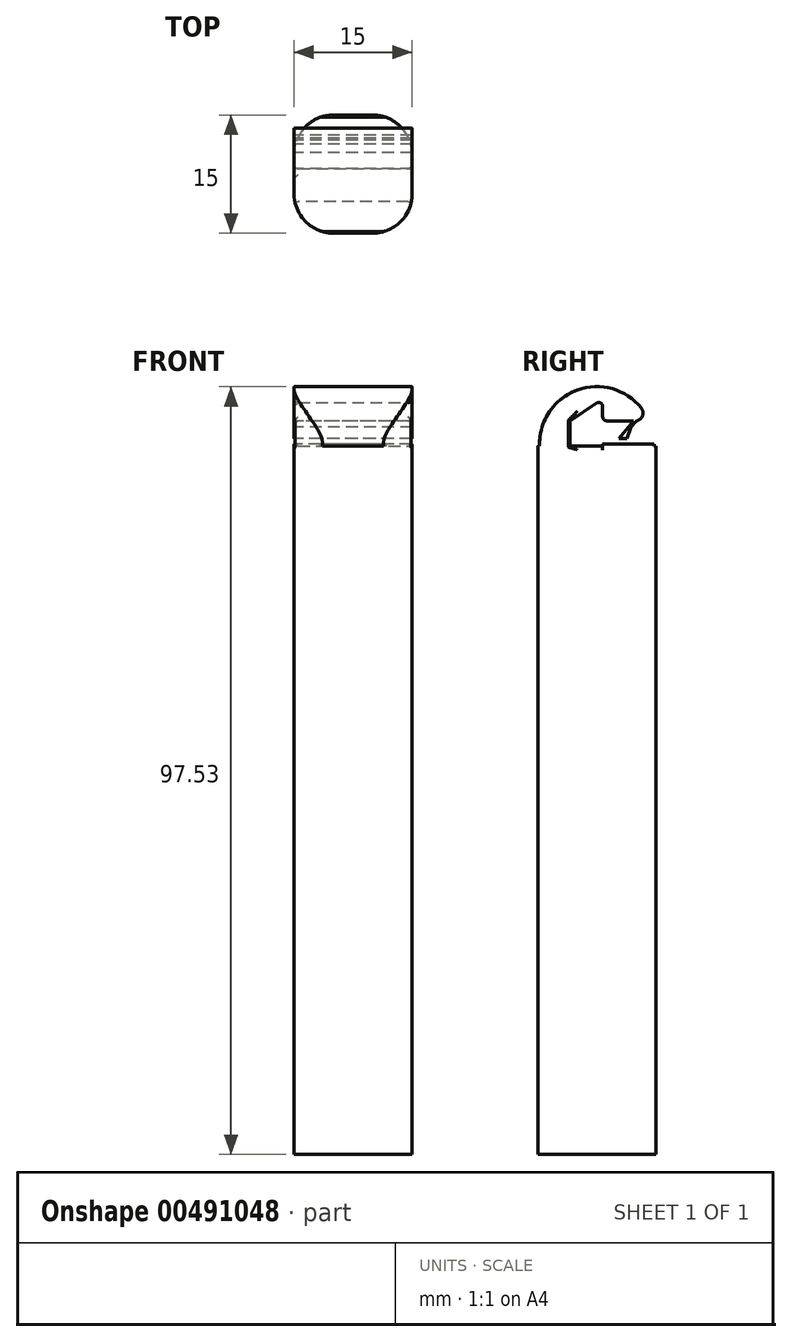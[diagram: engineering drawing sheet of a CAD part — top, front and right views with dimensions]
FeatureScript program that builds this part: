
annotation { "Feature Type Name" : "Feature", "Feature Type Description" : "" }
export const myFeature = defineFeature(function(context is Context, id is Id, definition is map)
    precondition{}
    {
        {
            var Q0;
            Q0=qCreatedBy(makeId("Front.planeOp"),FACE);
            var sketch = newSketch(context, id + "F0", { "sketchPlane" : qUnion([Q0])});
            skLineSegment(sketch, "E0.bottom", {"start": v(-7.5, 45) * mm, "end": v(7.5, 45) * mm});
            skLineSegment(sketch, "E0.top", {"start": v(-7.5, -45) * mm, "end": v(7.5, -45) * mm});
            skLineSegment(sketch, "E0.left", {"start": v(-7.5, 45) * mm, "end": v(-7.5, -45) * mm});
            skLineSegment(sketch, "E0.right", {"start": v(7.5, 45) * mm, "end": v(7.5, -45) * mm});
            skPoint(sketch, "E0.middle", {"position": v(0, 0) * mm});
            skSolve(sketch);
        }
        {
            var Q0;
            Q0 = qSketchRegion(id + "F0", true);
            extrude(context, id + "F1", {"entities" : qUnion([Q0]), "depth" : 15 * mm});
        }
        {
            var Q0;
            Q0=qCreatedBy(makeId("Right.planeOp"),FACE);
            var sketch = newSketch(context, id + "F2", { "sketchPlane" : qUnion([Q0])});
            skCircle(sketch, "E1", {"center": v(-7.55, 45.27) * mm, "radius": 7.26 * mm});
            skLineSegment(sketch, "E2", {"start": v(-0.9, 48.2) * mm, "end": v(-6.8, 48.2) * mm});
            skLineSegment(sketch, "E3", {"start": v(-6.8, 48.2) * mm, "end": v(-6.8, 50.95) * mm});
            skLineSegment(sketch, "E4", {"start": v(-6.8, 50.95) * mm, "end": v(-10.96, 48.2) * mm});
            skLineSegment(sketch, "E5", {"start": v(-10.96, 48.2) * mm, "end": v(-10.96, 43.94) * mm});
            skLineSegment(sketch, "E6", {"start": v(-10.96, 43.94) * mm, "end": v(-6.8, 43.94) * mm});
            skLineSegment(sketch, "E7", {"start": v(-6.8, 43.94) * mm, "end": v(-6.8, 45.27) * mm});
            skLineSegment(sketch, "E8", {"start": v(-6.8, 45.27) * mm, "end": v(0, 45.27) * mm});
            skLineSegment(sketch, "E9", {"start": v(0, 45.27) * mm, "end": v(-0.9, 48.2) * mm});
            skPoint(sketch, "E10.middle", {"position": v(-2.53, 48.66) * mm});
            skPoint(sketch, "E10.cornerSnap0", {"position": v(-6.8, 49.57) * mm});
            skPoint(sketch, "E11.orphan", {"position": v(-3.7, 49.57) * mm});
            skPoint(sketch, "E10.right.start.orphan", {"position": v(-1.37, 49.57) * mm});
            skPoint(sketch, "E10.left.end.orphan", {"position": v(-3.7, 47.75) * mm});
            skPoint(sketch, "E12.trimOffspring.end.orphan", {"position": v(-1.37, 47.75) * mm});
            skLineSegment(sketch, "E13", {"start": v(-2.9, 48.2) * mm, "end": v(-4.76, 45.96) * mm});
            skLineSegment(sketch, "E14", {"start": v(-4.76, 45.96) * mm, "end": v(-3.7, 45.96) * mm});
            skLineSegment(sketch, "E15", {"start": v(-3.7, 45.96) * mm, "end": v(-2.9, 48.2) * mm});
            skLineSegment(sketch, "E16", {"start": v(-2.53, 48.2) * mm, "end": v(-3.7, 46.79) * mm});
            skSolve(sketch);
        }
        {
            var Q0;
            {var subQ0=sQuery(id+"F2.wireOp",EDGE,"E2");Q0=makeQuery(id+"F2.imprint","IMPRINT",FACE,{"disambiguationData":[TD([[makeQuery(id+"F2.imprint","IMPRINT",EDGE,{"derivedFrom":subQ0}),-1.0]])]});}
            extrude(context, id + "F3", {"entities" : qUnion([Q0]), "operationType" : NewBodyOperationType.ADD, "endBound" : BoundingType.SYMMETRIC, "depth" : 15 * mm});
        }
        {
            var Q0;
            {var subQ0=sQuery(id+"F2.wireOp",EDGE,"E13");Q0=makeQuery(id+"F2.imprint","IMPRINT",FACE,{"disambiguationData":[TD([[makeQuery(id+"F2.imprint","IMPRINT",EDGE,{"derivedFrom":subQ0}),1.0]])]});}
            var Q1;
            {var subQ1=sQuery(id+"F2.wireOp",EDGE,"E2");var subQ3=sQuery(id+"F2.wireOp",EDGE,"E16");var subQ4=makeQuery(id+"F2.imprint","INTERSECT",VERTEX,{"derivedFrom":[subQ1,subQ3]});Q1=makeQuery(id+"F2.imprint","IMPRINT",FACE,{"disambiguationData":[TD([[makeQuery(id+"F2.imprint","IMPRINT",EDGE,{"disambiguationData":[TD([[subQ4,-1.0]])],"derivedFrom":subQ3}),-1.0]])]});}
            extrude(context, id + "F4", {"entities" : qUnion([Q0, Q1]), "operationType" : NewBodyOperationType.ADD, "endBound" : BoundingType.SYMMETRIC, "depth" : 15 * mm});
        }
        {
            var Q0;
            Q0=makeQuery(id+"F3.opExtrude","CAP_EDGE",EDGE,{"disambiguationData":[OSD([sQuery(id+"F2.wireOp",EDGE,"E4")])],"isStart":false});
            var Q1;
            Q1=makeQuery(id+"F3.opExtrude","CAP_EDGE",EDGE,{"disambiguationData":[OSD([sQuery(id+"F2.wireOp",EDGE,"E5")])],"isStart":false});
            var Q2;
            {var subQ0=sQuery(id+"F2.wireOp",EDGE,"E5");var subQ2=sQuery(id+"F0.wireOp",EDGE,"E0.right");var subQ3=sQuery(id+"F0.wireOp",EDGE,"E0.bottom");Q2=makeQuery(id+"F3.boolean.opBoolean","SPLIT",EDGE,{"disambiguationData":[TD([makeQuery(id+"F3.opExtrude","SWEPT_FACE",FACE,{"disambiguationData":[OSD([subQ0])]})])],"derivedFrom":makeQuery(id+"F1.opExtrude","SWEPT_EDGE",EDGE,{"disambiguationData":[OSD([subQ3,subQ2])]})});}
            var Q3;
            Q3=makeQuery(id+"F3.opExtrude","SWEPT_FACE",FACE,{"disambiguationData":[OSD([sQuery(id+"F2.wireOp",EDGE,"E3")])]});
            fillet(context, id + "F5", {"entities" : qUnion([Q0, Q1, Q2, Q3]), "radius" : 0.5 * mm, "tangentPropagation" : true, "allowEdgeOverflow" : false});
        }
        {
            var Q0;
            {var subQ0=sQuery(id+"F2.wireOp",EDGE,"E5");var subQ2=sQuery(id+"F0.wireOp",EDGE,"E0.left");var subQ3=sQuery(id+"F0.wireOp",EDGE,"E0.bottom");Q0=makeQuery(id+"F3.boolean.opBoolean","SPLIT",EDGE,{"disambiguationData":[TD([makeQuery(id+"F3.opExtrude","SWEPT_FACE",FACE,{"disambiguationData":[OSD([subQ0])]})])],"derivedFrom":makeQuery(id+"F1.opExtrude","SWEPT_EDGE",EDGE,{"disambiguationData":[OSD([subQ3,subQ2])]})});}
            var Q1;
            Q1=makeQuery(id+"F3.opExtrude","CAP_EDGE",EDGE,{"disambiguationData":[OSD([sQuery(id+"F2.wireOp",EDGE,"E5")])],"isStart":true});
            fillet(context, id + "F6", {"entities" : qUnion([Q0, Q1]), "radius" : 0.5 * mm, "tangentPropagation" : true, "allowEdgeOverflow" : false});
        }
        {
            var Q0;
            Q0=makeQuery(id+"F3.opExtrude","SWEPT_EDGE",EDGE,{"disambiguationData":[OSD([sQuery(id+"F2.wireOp",EDGE,"E1"),sQuery(id+"F2.wireOp",EDGE,"E2"),sQuery(id+"F2.wireOp",EDGE,"E9")])]});
            fillet(context, id + "F7", {"entities" : qUnion([Q0]), "radius" : 1 * mm, "tangentPropagation" : true, "allowEdgeOverflow" : false});
        }
        {
            var Q0;
            Q0=makeQuery(id+"F1.opExtrude","CAP_EDGE",EDGE,{"disambiguationData":[OSD([sQuery(id+"F0.wireOp",EDGE,"E0.left")])],"isStart":true});
            var Q1;
            Q1=makeQuery(id+"F1.opExtrude","CAP_EDGE",EDGE,{"disambiguationData":[OSD([sQuery(id+"F0.wireOp",EDGE,"E0.left")])],"isStart":false});
            var Q2;
            Q2=makeQuery(id+"F1.opExtrude","CAP_EDGE",EDGE,{"disambiguationData":[OSD([sQuery(id+"F0.wireOp",EDGE,"E0.right")])],"isStart":false});
            var Q3;
            Q3=makeQuery(id+"F1.opExtrude","CAP_EDGE",EDGE,{"disambiguationData":[OSD([sQuery(id+"F0.wireOp",EDGE,"E0.right")])],"isStart":true});
            fillet(context, id + "F8", {"entities" : qUnion([Q0, Q1, Q2, Q3]), "radius" : 5 * mm, "tangentPropagation" : true, "allowEdgeOverflow" : false});
        }
    });
